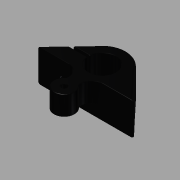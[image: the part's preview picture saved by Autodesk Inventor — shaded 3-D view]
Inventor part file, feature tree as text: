
AUTODESK INVENTOR PART (.ipt)
format: ipt  version: 2014 (Build 180170000, 170)  size: 469,504 bytes
history: native  units: mm
features: sketch x10, fillet x9, extrude x7, projected_geometry x6, plane x1
ambient origin geometry x8: Origin, YZ Plane, XZ Plane, XY Plane, X Axis, Y Axis, Z Axis, Center Point
bodies: Body1 (feature_tree)
feature tree (33):
  extrude  "Extrusion2"  Depth=226.0mm
  sketch  "Sketch2"  dims[d2=110.0mm d3=25.4mm d5=26.0mm]
  extrude  "Extrusion6"  Depth=25.4mm
  fillet  "Fillet2"  Radius=26.0mm
  extrude  "Extrusion11"  Depth=20.0mm
  extrude  "Extrusion12"  Depth=25.0mm
  extrude  "Extrusion13"  Depth=25.0mm
  plane  "Work Plane7"
  extrude  "Extrusion14"  Depth=25.0mm
  fillet  "Fillet7"  Radius=22.0mm
  fillet  "Fillet8"  Radius=30.0mm
  fillet  "Fillet9"  Radius=30.0mm
  fillet  "Fillet10"  Radius=20.0mm
  fillet  "Fillet11"  Radius=6.0mm
  fillet  "Fillet12"  Radius=5.0mm
  fillet  "Fillet13"  Radius=5.0mm
  sketch  "Sketch15"  dims[d49=14.0mm]
  sketch  "Sketch16"  dims[d50=6.5mm]
  sketch  "Sketch17"  dims[d51=13.0mm d52=1.2mm d53=1.2mm d54=5.0mm d55=18.0mm d56=0.0mm d57=10.0mm d81=2.5mm d82=30.0mm d83=0.0mm d84=9.0mm d87=30.0mm d88=0.0mm d89=3.5mm d90=30.0mm d91=20.0mm d92=0.0mm d93=0.0mm d94=-5.0mm d95=7.5mm d96=30.0mm d97=0.0mm d99=1.0mm d100=2.0mm d101=0.5mm d102=2000.0mm d103=20.0mm d104=1.0mm d105=0.5mm d107=3.85mm d108=5.3mm d109=35.0mm d110=10.0mm d111=0.0mm d112=0.2mm]
  extrude  "Extrusion15"  Depth=19.0mm
  fillet  "Fillet15"  Radius=7.0mm
  sketch  "Sketch1"  dims[d0=113.0mm d1=226.0mm]
  projected_geometry  "Projected Loop1"
  sketch  "Sketch4"  dims[d14=20.0mm d17=20.0mm]
  projected_geometry  "Projected Loop3"
  sketch  "Sketch10"  dims[d18=20.0mm d19=25.0mm]
  projected_geometry  "Projected Loop7"
  sketch  "Sketch11"  dims[d20=20.0mm d21=25.0mm]
  sketch  "Sketch12"  dims[d22=25.0mm d23=25.0mm d24=22.0mm d27=30.0mm d28=0.0mm d33=30.0mm d34=20.0mm d35=6.0mm d41=5.0mm d42=5.0mm]
  projected_geometry  "Projected Loop8"
  sketch  "Sketch13"  dims[d46=35.0mm d47=19.0mm d48=7.0mm]
  projected_geometry  "Projected Loop9"
  projected_geometry  "Projected Loop10"
